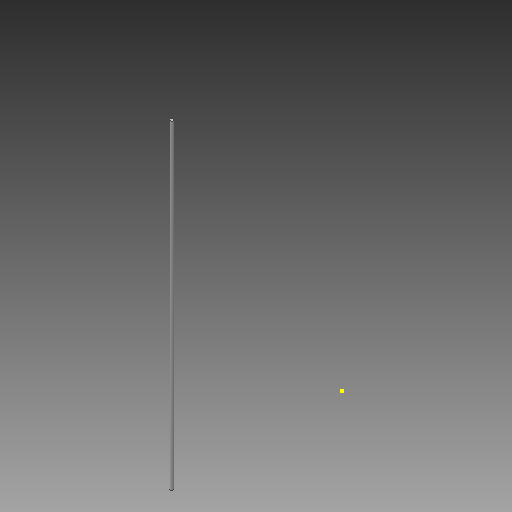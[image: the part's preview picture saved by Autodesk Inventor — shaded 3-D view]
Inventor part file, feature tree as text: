
AUTODESK INVENTOR PART (.ipt)
format: ipt  version: 2017 (Build 210142000, 142)  size: 75,776 bytes
history: native  units: mm
features: sketch x2, extrude x1, thread x1
ambient origin geometry x8: Origin, YZ Plane, XZ Plane, XY Plane, X Axis, Y Axis, Z Axis, Center Point
bodies: Solid1 (feature_tree)
feature tree (4):
  sketch  "Sketch1"  dims[d0=8.0mm d1=800.0mm d2=0.0mm d3=10.0mm d4=0.0mm]
  extrude  "Extrusion1"  Depth=800.0mm TaperAngle=0.0deg
  thread  "Thread1"  [1 undecoded]
  sketch  "Sketch2"
note: 1 required parameter value undecoded (feature->parameter linkage not recoverable at this tier; creation-order binding heuristic only, values carry confidence <= 0.55)
